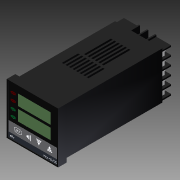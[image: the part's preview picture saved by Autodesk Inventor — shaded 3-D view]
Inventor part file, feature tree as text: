
AUTODESK INVENTOR PART (.ipt)
format: ipt  version: 2012 (Build 160160000, 160)  size: 1,552,896 bytes
history: native  units: in
note: dims shown in document units (in); Inventor stores cm internally (conversion verified against a paired STEP export)
features: sketch x27, extrude x25, projected_geometry x5, emboss x3, chamfer x1, fillet x1, pattern_linear x1
ambient origin geometry x8: Origin, YZ Plane, XZ Plane, XY Plane, X Axis, Y Axis, Z Axis, Center Point
bodies: Solid1 (feature_tree)
feature tree (63):
  extrude  "Extrusion1"  Depth=1.873in
  extrude  "Extrusion2"  Depth=0.04in
  extrude  "Extrusion3"  Depth=1.733in
  extrude  "Extrusion4"  Depth=1.2in
  extrude  "Extrusion5"  Depth=0.28in
  emboss  "Emboss1"
  extrude  "Extrusion6"  Depth=0.4in
  extrude  "Extrusion7"  Depth=0.18in
  sketch  "Sketch9"  dims[d20=0.05in d21=0.25in]
  extrude  "Extrusion8"  Depth=0.08in
  emboss  "Emboss2"
  extrude  "Extrusion9"  Depth=0.25in
  emboss  "Emboss3"
  extrude  "Extrusion10"  Depth=0.0001in TaperAngle=0.0deg
  extrude  "Extrusion11"  Depth=0.54in
  extrude  "Extrusion12"  Depth=0.215in
  extrude  "Extrusion13"  Depth=0.3in
  extrude  "Extrusion14"  Depth=0.17in
  extrude  "Extrusion15"  Depth=0.0001in TaperAngle=0.0deg
  extrude  "Extrusion16"  Depth=0.2in
  extrude  "Extrusion17"  Depth=0.2in
  extrude  "Extrusion18"  Depth=0.025in
  extrude  "Extrusion19"  Depth=0.045in
  chamfer  "Chamfer1"  Distance=0.0002in
  extrude  "Extrusion20"  Depth=0.325in
  extrude  "Extrusion21"  Depth=0.0625in TaperAngle=0.0deg
  extrude  "Extrusion22"  Depth=0.05in
  fillet  "Fillet1"  Radius=0.05in
  pattern_linear  "Rectangular Pattern1"  Spacing1=0.05in  [1 undecoded]
  extrude  "Extrusion23"  Depth=0.25in
  extrude  "Extrusion24"  Depth=0.25in
  extrude  "Extrusion25"  Depth=0.0625in TaperAngle=0.0deg
  sketch  "Sketch1"  dims[d0=1.883in d1=1.873in]
  sketch  "Sketch2"  dims[d2=0.312in d3=0.0in d4=0.04in]
  sketch  "Sketch3"  dims[d5=0.025in d6=0.0in d7=1.733in]
  sketch  "Sketch4"  dims[d8=3.915in d9=0.0in d10=1.2in]
  sketch  "Sketch5"  dims[d11=0.3in d12=0.28in]
  sketch  "Sketch6"  dims[d13=0.09in d14=0.4in]
  sketch  "Sketch7"  dims[d15=0.0001in d16=0.0in d17=0.18in]
  sketch  "Sketch8"  dims[d18=0.18in d19=0.08in]
  sketch  "Sketch10"  dims[d22=0.25in d23=0.0001in d24=0.0in]
  sketch  "Sketch11"  dims[d25=0.0005in d26=0.0in d27=0.54in]
  sketch  "Sketch12"  dims[d28=0.0005in d29=0.0in d30=0.215in]
  sketch  "Sketch13"  dims[d31=0.0001in d32=0.0in d33=0.3in]
  sketch  "Sketch14"  dims[d34=0.235in d35=0.17in]
  projected_geometry  "Projected Loop1"
  sketch  "Sketch15"  dims[d36=0.01in d37=0.0001in d38=0.0in]
  sketch  "Sketch16"  dims[d39=0.0005in d40=0.0in d41=0.2in]
  sketch  "Sketch17"  dims[d42=0.675in d43=0.2in]
  projected_geometry  "Projected Loop2"
  sketch  "Sketch18"  dims[d44=0.2in d45=0.025in]
  sketch  "Sketch19"  dims[d46=0.015in d47=0.045in]
  sketch  "Sketch20"  dims[d48=0.015in]
  sketch  "Sketch21"  dims[d49=0.015in]
  sketch  "Sketch22"  dims[d50=0.015in]
  sketch  "Sketch23"  dims[d51=0.025in]
  projected_geometry  "Projected Loop3"
  sketch  "Sketch24"  dims[d52=0.015in]
  projected_geometry  "Projected Loop4"
  sketch  "Sketch25"  dims[d53=0.015in]
  sketch  "Sketch26"  dims[d54=0.025in d55=0.0002in d56=0.0in]
  sketch  "Sketch27"  dims[d57=0.0003in d58=0.0in d59=0.325in d60=0.0625in d61=0.0in d62=0.05in d63=0.05in d64=0.05in d65=0.25in d66=0.25in d67=0.0625in d68=0.0in d69=0.5in d70=0.0in d71=0.0625in d72=0.0in d73=0.05in d74=0.05in d75=0.05in d76=0.25in d77=0.25in d78=0.5in d79=0.0in d80=0.5in d81=0.0in d82=0.26in d83=0.05in d84=0.05in d85=0.05in d86=0.05in d87=0.5in d88=0.0in d89=0.5in d90=0.0in d91=0.55in d92=0.55in d93=0.12in d94=0.0in d95=0.236in d96=0.08in d97=0.12in d98=0.0in d99=0.015in d100=0.125in d101=45.0deg d102=0.3in d103=0.24in d104=0.185in d105=0.0in d106=0.21in d107=0.1in d108=0.0in d109=0.05in d110=30.0deg d111=0.05in d112=30.0deg d113=0.025in d114=0.05in d115=0.13in d116=0.025in d117=0.03in d118=0.0in d119=0.025in d120=1.9685in d122=0.307in d123=0.065in d124=0.595in d125=1.6in d126=0.35in d127=0.065in d128=0.065in d129=0.065in d131=0.065in d132=0.065in d133=0.065in d134=0.065in d135=0.25in d136=0.0in d137=0.9875in d138=0.09in d139=0.25in d140=0.0in d141=0.25in d142=0.0in]
  projected_geometry  "Projected Loop5"
note: 1 required parameter value undecoded (feature->parameter linkage not recoverable at this tier; creation-order binding heuristic only, values carry confidence <= 0.55)
